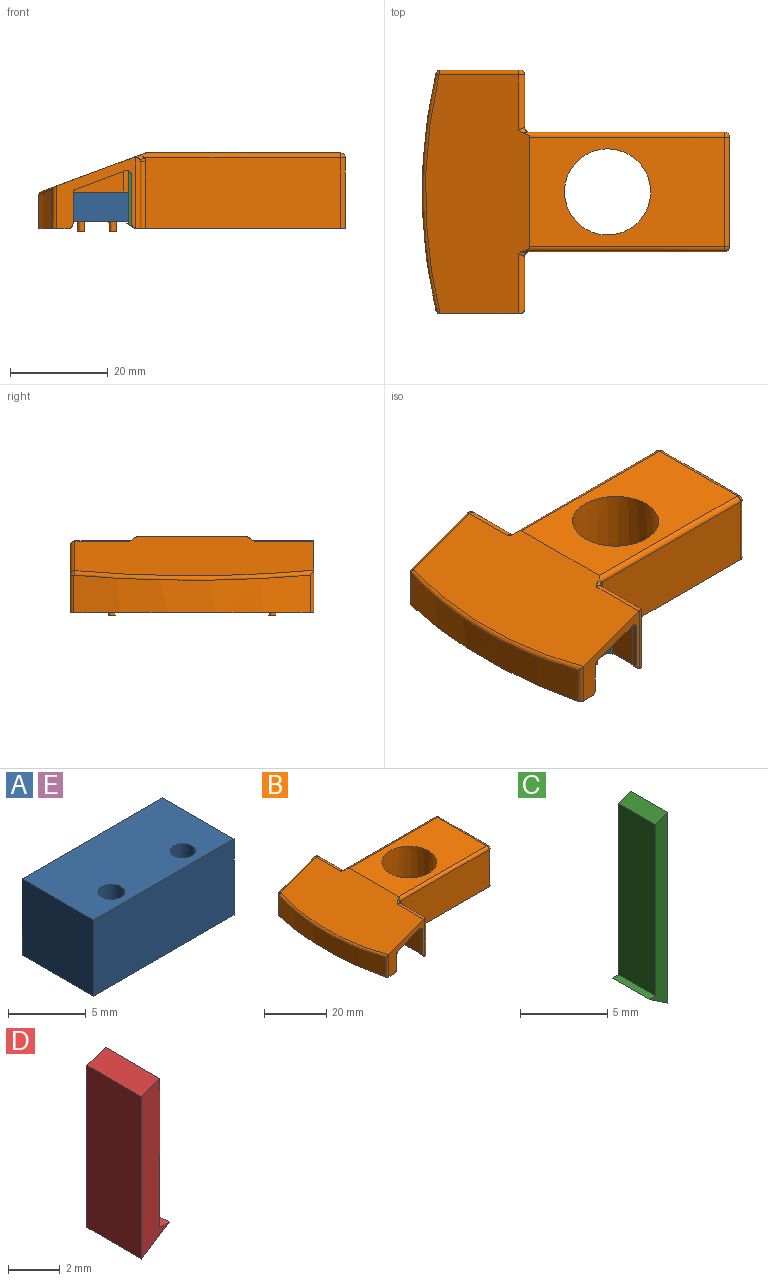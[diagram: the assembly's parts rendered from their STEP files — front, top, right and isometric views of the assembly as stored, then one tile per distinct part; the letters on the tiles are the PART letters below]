
ASSEMBLY  parts=5 mates=4
PART A: 8 faces, bbox 12.8x6.5x6 mm
  f0: plane 6.5x6mm, normal (-1,0,0), area 39mm2, adj f1,f5,f6,f7
  f1: plane 12.8x6mm, normal (0,1,0), area 76.8mm2, adj f0,f2,f6,f7
  f2: plane 6.5x6mm, normal (1,0,0), area 39mm2, adj f1,f5,f6,f7
  f3: cylinder r=0.85mm len=6mm, axis (0,0,1), area 32mm2, adj f6,f7
  f4: cylinder r=0.8mm len=6mm, axis (0,0,1), area 30.2mm2, adj f6,f7
  f5: plane 12.8x6mm, normal (0,-1,0), area 76.8mm2, adj f0,f2,f6,f7
  f6: plane 12.8x6.5mm, normal (0,0,-1), area 78.9mm2, adj f0,f1,f2,f3,f4,f5
  f7: plane 12.8x6.5mm, normal (0,0,1), area 78.9mm2, adj f0,f1,f2,f3,f4,f5
PART B: 108 faces, bbox 63.6x50.8x16.6 mm
  f0: plane 4.78x0.77mm, normal (0.05,-1,0), area 3mm2, adj f1,f16,f103,f104,f105,f107
  f1: cylinder r=104.67mm len=46.44mm, axis (0,0,-1), area 322.8mm2, adj f0,f2,f16,f87,f92,f104,f106
  f2: plane 48.16x21.34mm, normal (0.35,0,-0.94), area 733.3mm2, adj f1,f6,f7,f19,f20,f21,f23,f24
  f3: plane 16.21x14.69mm, normal (0,-1,0), area 69.4mm2, adj f16,f18,f29,f30,f31,f57,f58,f64
  f4: plane 16.21x13.69mm, normal (0,1,0), area 52.1mm2, adj f16,f26,f27,f28,f59,f62,f63,f78
  f5: plane 49.98x42.87mm, normal (0,0,-1), area 130.1mm2, adj f11,f12,f13,f14,f15,f21,f22,f23
  f6: plane 14.42x13.32mm, normal (0,1,0), area 34.1mm2, adj f2,f16,f30,f31,f75,f76,f77,f91
  f7: plane 14.42x13.32mm, normal (0,-1,0), area 34.1mm2, adj f2,f16,f26,f27,f78,f79,f80,f87
  f8: plane 20.74x20.74mm, normal (0,0,-1), area 62.1mm2, adj f17,f25
  f9: plane 40x22.5mm, normal (0,0,1), area 655.1mm2, adj f17,f18,f50,f53,f54
  f10: cylinder r=105.67mm len=48.46mm, axis (0,0,-1), area 374.5mm2, adj f16,f62,f64,f66
  f11: plane 13.69x10.75mm, normal (1,0,0), area 147.2mm2, adj f5,f57,f58,f70
  f12: plane 40.17x14.5mm, normal (0,-1,0), area 580mm2, adj f5,f53,f56,f70,f71
  f13: plane 22.5x14.5mm, normal (1,0,0), area 326.3mm2, adj f5,f51,f54,f56
  f14: plane 40.17x14.5mm, normal (0,1,0), area 580mm2, adj f5,f50,f51,f67,f68
  f15: plane 13.69x10.75mm, normal (1,0,0), area 147.2mm2, adj f5,f59,f60,f67
  f16: plane 50x6.5mm, normal (0,0,-1), area 69.5mm2, adj f0,f1,f3,f4,f6,f7,f10,f62
  f17: cone r=9.37mm half-angle=2deg, axis (0,0,-1), area 886.8mm2, adj f8,f9
  f18: plane 49.59x21.94mm, normal (-0.35,0,0.94), area 1003.5mm2, adj f3,f9,f50,f53,f58,f60,f63,f64
  f19: plane 39.82x22.5mm, normal (0,0,-1), area 589.8mm2, adj f2,f21,f22,f23,f25,f88,f89
  f20: plane 13.68x10.75mm, normal (-1,0,0), area 147.1mm2, adj f2,f73,f74,f91
  f21: plane 40x14.5mm, normal (0,1,0), area 579.7mm2, adj f2,f5,f19,f73,f88
  f22: plane 20.5x14.5mm, normal (-1,0,0), area 297.3mm2, adj f5,f19,f88,f89
  f23: plane 40x14.5mm, normal (0,-1,0), area 579.7mm2, adj f2,f5,f19,f81,f89
  f24: plane 13.68x10.75mm, normal (-1,0,0), area 147.1mm2, adj f2,f81,f82,f90
  f25: cone r=10.37mm half-angle=2deg, axis (0,0,-1), area 922.4mm2, adj f8,f19
  f26: plane 6.16x1mm, normal (1,0,0), area 6.2mm2, adj f4,f7,f79,f80
  f27: plane 10x3.72mm, normal (0.35,0,-0.94), area 10.7mm2, adj f4,f7,f78,f79
  f28: plane 9.88x1.01mm, normal (-1,0,0), area 10mm2, adj f4,f78,f82,f90
  f29: plane 9.88x1.01mm, normal (-1,0,0), area 10mm2, adj f3,f74,f75,f91
  f30: plane 10x3.72mm, normal (0.35,0,-0.94), area 10.7mm2, adj f3,f6,f75,f77
  f31: plane 6.16x1mm, normal (1,0,0), area 6.2mm2, adj f3,f6,f76,f77
  f32: plane 7x0.8mm, normal (-1,0,0), area 5.6mm2, adj f2,f33,f35,f36
  f33: plane 12x5.26mm, normal (0,-1,0), area 36.3mm2, adj f2,f32,f36,f85
  f34: plane 5.63x5mm, normal (1,0,0), area 28.2mm2, adj f2,f36,f85,f86
  f35: plane 12x5.26mm, normal (0,1,0), area 36.3mm2, adj f2,f32,f36,f86
  f36: plane 13x7mm, normal (0,0,-1), area 86mm2, adj f32,f33,f34,f35,f42,f44,f85,f86
  f37: plane 12x5.26mm, normal (0,-1,0), area 36.3mm2, adj f2,f40,f41,f83
  f38: plane 5.63x5mm, normal (1,0,0), area 28.2mm2, adj f2,f41,f83,f84
  f39: plane 12x5.26mm, normal (0,1,0), area 36.3mm2, adj f2,f40,f41,f84
  f40: plane 7x0.8mm, normal (-1,0,0), area 5.6mm2, adj f2,f37,f39,f41
  f41: plane 13x7mm, normal (0,0,-1), area 86mm2, adj f37,f38,f39,f40,f46,f48,f83,f84
  f42: cone r=0.85mm half-angle=1deg, axis (0,0,1), area 39.2mm2, adj f36,f43
  f43: plane 1.42x1.42mm, normal (0,0,-1), area 1.6mm2, adj f42
  f44: cone r=0.85mm half-angle=1deg, axis (0,0,1), area 39.2mm2, adj f36,f45
  f45: plane 1.42x1.42mm, normal (0,0,-1), area 1.6mm2, adj f44
  f46: cone r=0.85mm half-angle=1deg, axis (0,0,1), area 39.2mm2, adj f41,f47
  f47: plane 1.42x1.42mm, normal (0,0,-1), area 1.6mm2, adj f46
  f48: cone r=0.85mm half-angle=1deg, axis (0,0,1), area 39.2mm2, adj f41,f49
  f49: plane 1.42x1.42mm, normal (0,0,-1), area 1.6mm2, adj f48
  f50: cylinder r=1mm len=41.27mm, axis (1,0,0), area 63.9mm2, adj f9,f14,f18,f52,f69
  f51: cylinder r=1mm len=14.5mm, axis (0,0,1), area 22.8mm2, adj f5,f13,f14,f52
  f52: sphere r=1mm, area 1mm2, adj f50,f51,f54
  f53: cylinder r=1mm len=41.27mm, axis (-1,0,0), area 63.9mm2, adj f9,f12,f18,f55,f72
  f54: cylinder r=1mm len=22.5mm, axis (0,-1,0), area 35.3mm2, adj f9,f13,f52,f55
  f55: sphere r=1mm, area 1.6mm2, adj f53,f54,f56
  f56: cylinder r=1mm len=14.5mm, axis (0,0,-1), area 22.8mm2, adj f5,f12,f13,f55
  f57: cylinder r=1mm len=14.69mm, axis (0,0,1), area 22.5mm2, adj f3,f5,f11,f58,f74
  f58: cylinder r=1mm len=12.06mm, axis (0,-1,0), area 22.3mm2, adj f3,f11,f18,f57,f71,f72
  f59: cylinder r=1mm len=13.69mm, axis (0,0,-1), area 21.5mm2, adj f4,f5,f15,f61,f82
  f60: cylinder r=1mm len=11.06mm, axis (0,-1,0), area 20.9mm2, adj f15,f18,f61,f68,f69
  f61: sphere r=1mm, area 1.9mm2, adj f59,f60,f63
  f62: cylinder r=1mm len=7.66mm, axis (0,0,-1), area 10.3mm2, adj f4,f10,f16,f65
  f63: cylinder r=1mm len=16.56mm, axis (0.94,0,0.35), area 27.2mm2, adj f4,f18,f61,f65
  f64: cylinder r=1mm len=8.73mm, axis (0,0,-1), area 11.1mm2, adj f3,f10,f16,f18,f66
  f65: sphere r=1mm, area 0.7mm2, adj f62,f63,f66
  f66: bspline ~49.46x3.68mm, area 60mm2, adj f10,f18,f64,f65
  f67: cylinder r=1mm len=13.69mm, axis (0,0,-1), area 21.5mm2, adj f5,f14,f15,f68
  f68: torus R=2mm, axis (0,1,0), area 0.9mm2, adj f14,f60,f67,f69
  f69: bspline ~2.93x1.2mm, area 1.6mm2, adj f18,f50,f60,f68
  f70: cylinder r=1mm len=13.69mm, axis (0,0,1), area 21.5mm2, adj f5,f11,f12,f71
  f71: torus R=2mm, axis (0,1,0), area 0.9mm2, adj f12,f58,f70,f72
  f72: bspline ~2.93x1.2mm, area 1.6mm2, adj f18,f53,f58,f71
  f73: cylinder r=1mm len=14.06mm, axis (0,0,-1), area 21.8mm2, adj f2,f5,f20,f21,f74
  f74: cylinder r=1mm len=13.25mm, axis (0,1,0), area 3.4mm2, adj f3,f5,f20,f29,f57,f73,f91
  f75: cylinder r=1mm len=1.35mm, axis (0,1,0), area 1.9mm2, adj f3,f6,f29,f30,f91
  f76: cylinder r=1mm len=1mm, axis (0,1,0), area 1.6mm2, adj f3,f6,f16,f31
  f77: cylinder r=1mm len=1mm, axis (0,1,0), area 1.2mm2, adj f3,f6,f30,f31
  f78: cylinder r=1mm len=1.35mm, axis (0,1,0), area 1.9mm2, adj f4,f7,f27,f28,f90
  f79: cylinder r=1mm len=1mm, axis (0,1,0), area 1.2mm2, adj f4,f7,f26,f27
  f80: cylinder r=1mm len=1mm, axis (0,1,0), area 1.6mm2, adj f4,f7,f16,f26
  f81: cylinder r=1mm len=14.06mm, axis (0,0,1), area 21.8mm2, adj f2,f5,f23,f24,f82
  f82: cylinder r=1mm len=13.25mm, axis (0,1,0), area 3.4mm2, adj f4,f5,f24,f28,f59,f81,f90
  f83: cylinder r=1mm len=5.63mm, axis (0,0,-1), area 8.6mm2, adj f2,f37,f38,f41
  f84: cylinder r=1mm len=5.63mm, axis (0,0,1), area 8.6mm2, adj f2,f38,f39,f41
  f85: cylinder r=1mm len=5.63mm, axis (0,0,1), area 8.6mm2, adj f2,f33,f34,f36
  f86: cylinder r=1mm len=5.63mm, axis (0,0,-1), area 8.6mm2, adj f2,f34,f35,f36
  f87: cylinder r=1mm len=7.96mm, axis (0,0,-1), area 10.5mm2, adj f1,f2,f7,f16
  f88: cylinder r=1mm len=14.5mm, axis (0,0,1), area 22.8mm2, adj f5,f19,f21,f22
  f89: cylinder r=1mm len=14.5mm, axis (0,0,-1), area 22.8mm2, adj f5,f19,f22,f23
  f90: cylinder r=1mm len=13.68mm, axis (0,0,1), area 19.5mm2, adj f2,f7,f24,f28,f78,f82
  f91: cylinder r=1mm len=13.68mm, axis (0,0,-1), area 19.5mm2, adj f2,f6,f20,f29,f74,f75
  f92: cylinder r=1mm len=7.96mm, axis (0,0,-1), area 10.5mm2, adj f1,f2,f6,f16
  f93: plane 8x3mm, normal (0,0,-1), area 24mm2, adj f94,f95,f96,f97
  f94: plane 8.24x3mm, normal (-1,0,0), area 24.7mm2, adj f2,f93,f95,f97
  f95: plane 11.21x8mm, normal (0,-1,0), area 77.8mm2, adj f2,f93,f94,f96
  f96: plane 11.21x3mm, normal (1,0,0), area 33.6mm2, adj f2,f93,f95,f97
  f97: plane 11.21x8mm, normal (0,1,0), area 77.8mm2, adj f2,f93,f94,f96
  f98: plane 8x3mm, normal (0,0,-1), area 24mm2, adj f99,f100,f101,f102
  f99: plane 8.24x3mm, normal (-1,0,0), area 24.7mm2, adj f2,f98,f100,f102
  f100: plane 11.21x8mm, normal (0,-1,0), area 77.8mm2, adj f2,f98,f99,f101
  f101: plane 11.21x3mm, normal (1,0,0), area 33.6mm2, adj f2,f98,f100,f102
  f102: plane 11.21x8mm, normal (0,1,0), area 77.8mm2, adj f2,f98,f99,f101
  f103: plane 3x0.5mm, normal (1,0,0), area 1.5mm2, adj f0,f104,f105,f106
  f104: plane 4.78x3.48mm, normal (0.05,0,1), area 14.8mm2, adj f0,f1,f103,f106
  f105: plane 3.02x0.29mm, normal (0.05,0,-1), area 0.4mm2, adj f0,f103,f107
  f106: plane 4.31x0.73mm, normal (0.05,1,0), area 2.6mm2, adj f1,f16,f103,f104
  f107: plane 3.02x0.29mm, normal (-0.12,0.01,0.99), area 0.2mm2, adj f0,f16,f105
PART C: 7 faces, bbox 1.5x3x13.4 mm
  f0: plane 13.37x3mm, normal (1,0,0), area 40.1mm2, adj f1,f4,f5,f6
  f1: plane 3x1mm, normal (-0.35,0,0.94), area 3.2mm2, adj f0,f2,f5,f6
  f2: plane 12x3mm, normal (-1,0,0), area 36mm2, adj f1,f3,f5,f6
  f3: plane 3x0.5mm, normal (0,0,1), area 1.5mm2, adj f2,f4,f5,f6
  f4: plane 3x1.5mm, normal (-0.55,0,-0.83), area 5.4mm2, adj f0,f3,f5,f6
  f5: plane 13.37x1.5mm, normal (0,1,0), area 12.9mm2, adj f0,f1,f2,f3,f4
  f6: plane 13.37x1.5mm, normal (0,-1,0), area 12.9mm2, adj f0,f1,f2,f3,f4
PART D: 7 faces, bbox 1.5x3x8.1 mm
  f0: plane 7.06x3mm, normal (1,0,0), area 21.2mm2, adj f1,f4,f5,f6
  f1: plane 3x1mm, normal (-0.35,0,0.94), area 3.2mm2, adj f0,f2,f5,f6
  f2: plane 7.69x3mm, normal (-1,0,0), area 23.1mm2, adj f1,f3,f5,f6
  f3: plane 3x1.5mm, normal (0.55,0,-0.83), area 5.4mm2, adj f2,f4,f5,f6
  f4: plane 3x0.5mm, normal (0,0,1), area 1.5mm2, adj f0,f3,f5,f6
  f5: plane 8.06x1.5mm, normal (0,1,0), area 7.6mm2, adj f0,f1,f2,f3,f4
  f6: plane 8.06x1.5mm, normal (0,-1,0), area 7.6mm2, adj f0,f1,f2,f3,f4
PART E: same geometry as A
PLACE A t=(-10.1,3.09,-2.32)mm
PLACE B t=(-10.1,3.09,-7.32)mm fixed
PLACE C t=(-10.3,4.09,-7.39)mm
PLACE D t=(-10.01,4.09,-7.28)mm
PLACE E rot(axis=(0,0,1),180deg) t=(-70.1,3.09,-2.32)mm
MATE fastened B.f48 <-> E.f4  axis (0,0,-1) through (-43.35,19.59,0.18)mm
MATE fastened C.f2 <-> B.f34  axis (-1,0,0) through (-33.6,-12.91,5.82)mm
MATE fastened B.f42 <-> A.f3  axis (0,0,-1) through (-43.35,-13.41,0.18)mm
MATE fastened D.f0 <-> B.f32  axis (1,0,0) through (-46.6,-12.91,0.98)mm
